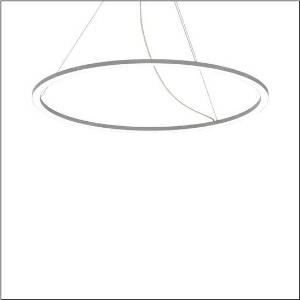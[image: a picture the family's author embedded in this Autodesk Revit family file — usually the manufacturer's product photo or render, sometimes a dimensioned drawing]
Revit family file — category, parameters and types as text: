
# Revit family: silica_r__21_ring-d_5pjbd4d3204a_8650
name_source: partatom
category: Lighting Fixtures
units: mm (PartAtom-declared; Revit-internal decimal feet)

## family parameters
Cut with Voids When Loaded = No
Host = Face
Light Source = No
Part Type = Normal
Room Calculation Point = No
Round Connector Dimension = Use Diameter
Shared = No

## types (1)
- Silica® 21 Ring-D (1 x LED, 11350 lm, 125 W, 4000K)
    Apparent Load = 125 VA
    CIE Flux Codes = 37 69 92 100 100
    Color Rendering = 80
    Color Temperature = 4000K
    Default Elevation = 1800 mm
    Description = Silica® 21 Ring-D, suspended luminaire, of PMMA, frosted, light emission: ring underside luminous distribution, primary light characteristic: symmetric, installation type: suspended mounting, LED, rated luminous flux: 11.350lm, luminous efficacy: 91lm/W, light colour: 840, colour temperature: 4000K, control gear: DALI 2, with terminal, 5-pole, mains connection: 230V, AC/DC, 0/50..60Hz, rated input power: 125W, housing, of extruded aluminium section, metallic grey (RAL 9006), diameter: 1.450mm, ceiling canopy, metallic grey (RAL 9006), protection rating (lamp compartment): IP40, insulation class (complete): insulation class I (protective earthing), certification: CE, impact resistance: IK02, permissible operating ambient temperature: 0..+35°C, packaging unit: 1 piece
    Height = 25 mm  [stored 0.082021 ft]
    Lamp = 1 x LED
    Lamp Light Flux = 11350 lm
    Lamp Power = 125 W
    Lamp count = 1
    Length = 1450 mm
    Luminous efficacy = 91 lm/W
    Manufacturer = Siteco
    ModVariant = No
    Model = 5PJBD4D3204A
    Mounting Place = Ceiling
    Mounting Type = Pendant
    Number of Poles = 1
    OnlyDefault = Yes
    Power Factor = 1
    Product Name = Silica® 21 Ring-D
    Product group = suspended luminaire
    ProductGroupID = 905
    Protection Class = Protection class I
    Protection Degree = IP 40
    RLX_Detail_Level = 1
    RLX_Emergency_Light_Flux = 0 lm
    RLX_Emergency_Type = 0
    RLX_Emergency_Type_DB = No
    RlxData = <blob elided: 17949 chars, md5=d41bc5f1>
    Socket = socket
    Standby Power = 0 W
    System Light Flux = 11350 lm
    System Power = 125 W
    Type Comments = Product without accessories
    Type Image = l_1251748.jpg
    URL = http://relux.com
    VarID = ---
    Voltage = 0 V
    Weight = 0.00 kg
    Width = 0 mm  [stored 0 ft]

note: [stored X ft] marks values corroborated as IEEE doubles in the binary element streams (Revit-internal decimal feet)

## geometry (parser evidence)
native form markers: Blend x4, Sweep x11
no freeform markers — native parametric forms only
